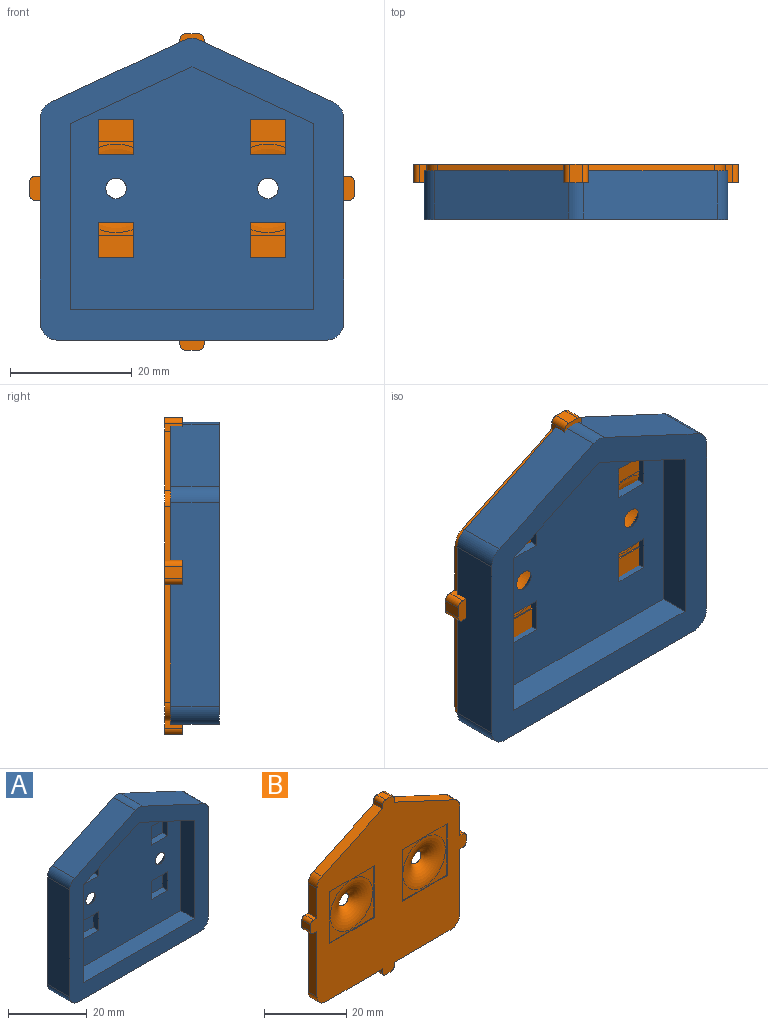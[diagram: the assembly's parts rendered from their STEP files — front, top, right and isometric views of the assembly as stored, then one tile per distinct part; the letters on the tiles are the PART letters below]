
ASSEMBLY  parts=2 mates=1
PART A: 50 faces, bbox 50x8x49.7 mm
  f0: plane 40x40mm, normal (0,-1,0), area 1260.8mm2, adj f17,f18,f19,f20,f21,f28,f29,f30
  f1: plane 50x49.69mm, normal (0,1,0), area 1728.8mm2, adj f2,f3,f4,f5,f6,f7,f8,f9
  f2: plane 22x10.26mm, normal (-0.42,0,0.91), area 194.2mm2, adj f1,f22,f23,f25
  f3: plane 33.43x8mm, normal (-1,0,0), area 267.4mm2, adj f1,f22,f23,f24
  f4: plane 44x8mm, normal (0,0,-1), area 352mm2, adj f1,f22,f24,f26
  f5: plane 33.43x8mm, normal (1,0,0), area 267.4mm2, adj f1,f22,f26,f27
  f6: plane 22x10.26mm, normal (0.42,0,0.91), area 194.2mm2, adj f1,f22,f25,f27
  f7: plane 15.4x0.2mm, normal (0,0,-1), area 3.1mm2, adj f1,f8,f10,f11
  f8: plane 15.4x0.2mm, normal (-1,0,0), area 3.1mm2, adj f1,f7,f9,f11
  f9: plane 15.4x0.2mm, normal (0,0,1), area 3.1mm2, adj f1,f8,f10,f11
  f10: plane 15.4x0.2mm, normal (1,0,0), area 3.1mm2, adj f1,f7,f9,f11
  f11: plane 15.4x15.4mm, normal (0,1,0), area 69.7mm2, adj f7,f8,f9,f10,f48
  f12: plane 15.4x0.2mm, normal (0,0,-1), area 3.1mm2, adj f1,f13,f15,f16
  f13: plane 15.4x0.2mm, normal (-1,0,0), area 3.1mm2, adj f1,f12,f14,f16
  f14: plane 15.4x0.2mm, normal (0,0,1), area 3.1mm2, adj f1,f13,f15,f16
  f15: plane 15.4x0.2mm, normal (1,0,0), area 3.1mm2, adj f1,f12,f14,f16
  f16: plane 15.4x15.4mm, normal (0,1,0), area 69.7mm2, adj f12,f13,f14,f15,f49
  f17: plane 40x5mm, normal (0,0,1), area 200mm2, adj f0,f18,f21,f22
  f18: plane 30.67x5mm, normal (1,0,0), area 153.4mm2, adj f0,f17,f19,f22
  f19: plane 20x9.33mm, normal (0.42,0,-0.91), area 110.3mm2, adj f0,f18,f20,f22
  f20: plane 20x9.33mm, normal (-0.42,0,-0.91), area 110.3mm2, adj f0,f19,f21,f22
  f21: plane 30.67x5mm, normal (-1,0,0), area 153.4mm2, adj f0,f17,f20,f22
  f22: plane 50x49.69mm, normal (0,-1,0), area 789.7mm2, adj f2,f3,f4,f5,f6,f17,f18,f19
  f23: cylinder r=3mm len=8mm, axis (0,-1,0), area 27.2mm2, adj f1,f2,f3,f22
  f24: cylinder r=3mm len=8mm, axis (0,1,0), area 37.7mm2, adj f1,f3,f4,f22
  f25: cylinder r=3mm len=8mm, axis (0,1,0), area 20.9mm2, adj f1,f2,f6,f22
  f26: cylinder r=3mm len=8mm, axis (0,-1,0), area 37.7mm2, adj f1,f4,f5,f22
  f27: cylinder r=3mm len=8mm, axis (0,1,0), area 27.2mm2, adj f1,f5,f6,f22
  f28: plane 5.8x2mm, normal (0,0,1), area 11.6mm2, adj f0,f29,f31,f32
  f29: plane 5.8x2mm, normal (-1,0,0), area 11.6mm2, adj f0,f28,f30,f32
  f30: plane 5.8x2mm, normal (0,0,-1), area 11.6mm2, adj f0,f29,f31,f32
  f31: plane 5.8x2mm, normal (1,0,0), area 11.6mm2, adj f0,f28,f30,f32
  f32: plane 5.8x5.8mm, normal (0,-1,0), area 33.6mm2, adj f28,f29,f30,f31
  f33: plane 5.8x2mm, normal (1,0,0), area 11.6mm2, adj f0,f34,f36,f37
  f34: plane 5.8x2mm, normal (0,0,1), area 11.6mm2, adj f0,f33,f35,f37
  f35: plane 5.8x2mm, normal (-1,0,0), area 11.6mm2, adj f0,f34,f36,f37
  f36: plane 5.8x2mm, normal (0,0,-1), area 11.6mm2, adj f0,f33,f35,f37
  f37: plane 5.8x5.8mm, normal (0,-1,0), area 33.6mm2, adj f33,f34,f35,f36
  f38: plane 5.8x2mm, normal (0,0,1), area 11.6mm2, adj f0,f39,f41,f42
  f39: plane 5.8x2mm, normal (-1,0,0), area 11.6mm2, adj f0,f38,f40,f42
  f40: plane 5.8x2mm, normal (0,0,-1), area 11.6mm2, adj f0,f39,f41,f42
  f41: plane 5.8x2mm, normal (1,0,0), area 11.6mm2, adj f0,f38,f40,f42
  f42: plane 5.8x5.8mm, normal (0,-1,0), area 33.6mm2, adj f38,f39,f40,f41
  f43: plane 5.8x2mm, normal (1,0,0), area 11.6mm2, adj f0,f44,f46,f47
  f44: plane 5.8x2mm, normal (0,0,1), area 11.6mm2, adj f0,f43,f45,f47
  f45: plane 5.8x2mm, normal (-1,0,0), area 11.6mm2, adj f0,f44,f46,f47
  f46: plane 5.8x2mm, normal (0,0,-1), area 11.6mm2, adj f0,f43,f45,f47
  f47: plane 5.8x5.8mm, normal (0,-1,0), area 33.6mm2, adj f43,f44,f45,f46
  f48: torus R=7.3mm, axis (0,1,0), area 174.6mm2, adj f0,f11
  f49: torus R=7.3mm, axis (0,1,0), area 174.6mm2, adj f0,f16
PART B: 66 faces, bbox 53.5x7.2x52.1 mm
  f0: plane 53.5x52.1mm, normal (0,-1,0), area 1659mm2, adj f2,f3,f4,f5,f6,f7,f8,f9
  f1: plane 53.5x52.1mm, normal (0,1,0), area 1980.6mm2, adj f2,f3,f4,f5,f6,f7,f8,f9
  f2: plane 19.55x3mm, normal (0,0,-1), area 58.6mm2, adj f0,f1,f3,f23
  f3: plane 3x1.2mm, normal (-1,0,0), area 3.6mm2, adj f0,f1,f2,f63
  f4: plane 3x2mm, normal (0,0,-1), area 6mm2, adj f0,f1,f62,f63
  f5: plane 3x1.2mm, normal (1,0,0), area 3.6mm2, adj f0,f1,f6,f62
  f6: plane 19.55x3mm, normal (0,0,-1), area 58.6mm2, adj f0,f1,f5,f24
  f7: plane 19.45x3mm, normal (1,0,0), area 58.3mm2, adj f0,f1,f8,f24
  f8: plane 3x1.2mm, normal (0,0,-1), area 3.6mm2, adj f0,f1,f7,f65
  f9: plane 3x2mm, normal (1,0,0), area 6mm2, adj f0,f1,f64,f65
  f10: plane 3x1.2mm, normal (0,0,1), area 3.6mm2, adj f0,f1,f11,f64
  f11: plane 8.82x3mm, normal (1,0,0), area 26.5mm2, adj f0,f1,f10,f25
  f12: plane 20.82x9.71mm, normal (0.42,0,0.91), area 68.9mm2, adj f0,f1,f13,f25
  f13: plane 3x1.2mm, normal (1,0,0), area 3.6mm2, adj f0,f1,f12,f59
  f14: plane 3x2mm, normal (0,0,1), area 6mm2, adj f0,f1,f58,f59
  f15: plane 3x1.2mm, normal (-1,0,0), area 3.6mm2, adj f0,f1,f16,f58
  f16: plane 20.82x9.71mm, normal (-0.42,0,0.91), area 68.9mm2, adj f0,f1,f15,f22
  f17: plane 8.82x3mm, normal (-1,0,0), area 26.5mm2, adj f0,f1,f18,f22
  f18: plane 3x1.2mm, normal (0,0,1), area 3.6mm2, adj f0,f1,f17,f60
  f19: plane 3x2mm, normal (-1,0,0), area 6mm2, adj f0,f1,f60,f61
  f20: plane 3x1.2mm, normal (0,0,-1), area 3.6mm2, adj f0,f1,f21,f61
  f21: plane 19.45x3mm, normal (-1,0,0), area 58.3mm2, adj f0,f1,f20,f23
  f22: cylinder r=3mm len=3mm, axis (0,-1,0), area 10.2mm2, adj f0,f1,f16,f17
  f23: cylinder r=3mm len=3mm, axis (0,1,0), area 14.1mm2, adj f0,f1,f2,f21
  f24: cylinder r=3mm len=3mm, axis (0,-1,0), area 14.1mm2, adj f0,f1,f6,f7
  f25: cylinder r=3mm len=3mm, axis (0,-1,0), area 10.2mm2, adj f0,f1,f11,f12
  f26: plane 5.8x2mm, normal (0,0,1), area 11.6mm2, adj f1,f27,f29,f30
  f27: plane 5.8x2mm, normal (1,0,0), area 11.6mm2, adj f1,f26,f28,f30
  f28: plane 5.8x2mm, normal (0,0,-1), area 11.6mm2, adj f1,f27,f29,f30
  f29: plane 5.8x2mm, normal (-1,0,0), area 11.6mm2, adj f1,f26,f28,f30
  f30: plane 5.8x5.8mm, normal (0,1,0), area 33.6mm2, adj f26,f27,f28,f29
  f31: plane 5.8x2mm, normal (0,0,-1), area 11.6mm2, adj f1,f32,f34,f35
  f32: plane 5.8x2mm, normal (-1,0,0), area 11.6mm2, adj f1,f31,f33,f35
  f33: plane 5.8x2mm, normal (0,0,1), area 11.6mm2, adj f1,f32,f34,f35
  f34: plane 5.8x2mm, normal (1,0,0), area 11.6mm2, adj f1,f31,f33,f35
  f35: plane 5.8x5.8mm, normal (0,1,0), area 33.6mm2, adj f31,f32,f33,f34
  f36: plane 5.8x2mm, normal (0,0,1), area 11.6mm2, adj f1,f37,f39,f40
  f37: plane 5.8x2mm, normal (1,0,0), area 11.6mm2, adj f1,f36,f38,f40
  f38: plane 5.8x2mm, normal (0,0,-1), area 11.6mm2, adj f1,f37,f39,f40
  f39: plane 5.8x2mm, normal (-1,0,0), area 11.6mm2, adj f1,f36,f38,f40
  f40: plane 5.8x5.8mm, normal (0,1,0), area 33.6mm2, adj f36,f37,f38,f39
  f41: plane 5.8x2mm, normal (0,0,-1), area 11.6mm2, adj f1,f42,f44,f45
  f42: plane 5.8x2mm, normal (-1,0,0), area 11.6mm2, adj f1,f41,f43,f45
  f43: plane 5.8x2mm, normal (0,0,1), area 11.6mm2, adj f1,f42,f44,f45
  f44: plane 5.8x2mm, normal (1,0,0), area 11.6mm2, adj f1,f41,f43,f45
  f45: plane 5.8x5.8mm, normal (0,1,0), area 33.6mm2, adj f41,f42,f43,f44
  f46: plane 15.4x0.2mm, normal (0,0,-1), area 3.1mm2, adj f0,f47,f49,f50
  f47: plane 15.4x0.2mm, normal (1,0,0), area 3.1mm2, adj f0,f46,f48,f50
  f48: plane 15.4x0.2mm, normal (0,0,1), area 3.1mm2, adj f0,f47,f49,f50
  f49: plane 15.4x0.2mm, normal (-1,0,0), area 3.1mm2, adj f0,f46,f48,f50
  f50: plane 15.4x15.4mm, normal (0,-1,0), area 69.7mm2, adj f46,f47,f48,f49,f56
  f51: plane 15.4x0.2mm, normal (0,0,-1), area 3.1mm2, adj f0,f52,f54,f55
  f52: plane 15.4x0.2mm, normal (1,0,0), area 3.1mm2, adj f0,f51,f53,f55
  f53: plane 15.4x0.2mm, normal (0,0,1), area 3.1mm2, adj f0,f52,f54,f55
  f54: plane 15.4x0.2mm, normal (-1,0,0), area 3.1mm2, adj f0,f51,f53,f55
  f55: plane 15.4x15.4mm, normal (0,-1,0), area 69.7mm2, adj f51,f52,f53,f54,f57
  f56: torus R=7.3mm, axis (0,-1,0), area 174.6mm2, adj f1,f50
  f57: torus R=7.3mm, axis (0,-1,0), area 174.6mm2, adj f1,f55
  f58: cylinder r=1mm len=3mm, axis (0,-1,0), area 4.7mm2, adj f0,f1,f14,f15
  f59: cylinder r=1mm len=3mm, axis (0,1,0), area 4.7mm2, adj f0,f1,f13,f14
  f60: cylinder r=1mm len=3mm, axis (0,-1,0), area 4.7mm2, adj f0,f1,f18,f19
  f61: cylinder r=1mm len=3mm, axis (0,1,0), area 4.7mm2, adj f0,f1,f19,f20
  f62: cylinder r=1mm len=3mm, axis (0,1,0), area 4.7mm2, adj f0,f1,f4,f5
  f63: cylinder r=1mm len=3mm, axis (0,-1,0), area 4.7mm2, adj f0,f1,f3,f4
  f64: cylinder r=1mm len=3mm, axis (0,-1,0), area 4.7mm2, adj f0,f1,f9,f10
  f65: cylinder r=1mm len=3mm, axis (0,1,0), area 4.7mm2, adj f0,f1,f8,f9
PLACE A t=(3.16,4.63,-6.42)mm
PLACE B t=(26.12,5.63,11.32)mm
MATE fastened B.f45 <-> A.f47  axis (0,1,0) through (23.27,3.63,17.38)mm
